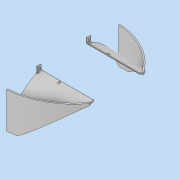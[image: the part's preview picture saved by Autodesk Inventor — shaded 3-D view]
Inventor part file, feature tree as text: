
AUTODESK INVENTOR PART (.ipt)
format: ipt  version: 2019 (Build 230136000, 136)  size: 896,000 bytes
history: native  units: mm
features: extrude x29, sketch x27, projected_geometry x12, fillet x5, other x4, mirror x3, loft x1, shell x1
ambient origin geometry x8: Origin, YZ Plane, XZ Plane, XY Plane, X Axis, Y Axis, Z Axis, Center Point
bodies: Body1 (feature_tree)
feature tree (82):
  sketch  "Эскиз4"
  other  "РабПлоскость1"
  sketch  "Эскиз5"
  loft  "Лофт1"
  extrude  "Выдавливание2"  Depth=100.0mm
  shell  "Оболочка1"  Thickness=17.0mm
  sketch  "Эскиз21"
  extrude  "Выдавливание15"  Depth=4.0mm
  extrude  "Выдавливание16"  Depth=35.0mm
  other  "РабПлоскость7"
  sketch  "Эскиз23"
  extrude  "Выдавливание17"  TaperAngle=0.0deg  [1 undecoded]
  extrude  "Выдавливание18"  TaperAngle=0.0deg  [1 undecoded]
  sketch  "Эскиз24"
  extrude  "Выдавливание19"  TaperAngle=0.0deg  [1 undecoded]
  extrude  "Выдавливание20"  Depth=130.0mm TaperAngle=0.0deg
  extrude  "Выдавливание21"  Depth=5.0mm
  mirror  "Зеркальное отражение2"
  other  "РабПлоскость12"
  extrude  "Выдавливание57"  Depth=2.0mm
  extrude  "Выдавливание62"  Depth=2.0mm
  mirror  "Зеркальное отражение5"
  extrude  "Выдавливание67"  Depth=2.0mm
  sketch  "Эскиз81"
  extrude  "Выдавливание68"  Depth=20.0mm
  extrude  "Выдавливание69"  Depth=10.0mm TaperAngle=0.0deg
  sketch  "Эскиз83"
  mirror  "Зеркальное отражение6"
  extrude  "Выдавливание70"  Depth=10.0mm TaperAngle=0.0deg
  sketch  "Эскиз84"
  extrude  "Выдавливание75"  Depth=143.802871mm
  extrude  "Выдавливание76"  TaperAngle=0.0deg  [1 undecoded]
  extrude  "Выдавливание77"  Depth=1.0mm TaperAngle=0.0deg
  extrude  "Выдавливание95"  Depth=5.0mm
  extrude  "Выдавливание96"  Depth=5.0mm
  extrude  "Выдавливание97"  Depth=2.0mm
  extrude  "Выдавливание98"  Depth=2.0mm
  extrude  "Выдавливание99"  Depth=5.0mm
  extrude  "Выдавливание100"  Depth=1.0mm TaperAngle=0.0deg
  extrude  "Выдавливание101"  Depth=3.0mm
  extrude  "Выдавливание102"  Depth=2.0mm
  extrude  "Выдавливание103"  Depth=6.0mm
  extrude  "Выдавливание104"  Depth=1.0mm TaperAngle=0.0deg
  fillet  "Сопряжение3"  Radius=2.0mm
  other  "РабПлоскость25"
  extrude  "Выдавливание105"  Depth=2.0mm
  extrude  "Выдавливание106"  Depth=2.0mm
  fillet  "Сопряжение4"  Radius=5.0mm
  fillet  "Сопряжение5"  Radius=1.0mm
  fillet  "Сопряжение6"  Radius=4.0mm
  fillet  "Сопряжение7"  Radius=2.0mm
  sketch  "Эскиз6"
  projected_geometry  "Спроецированная петля1"
  sketch  "Эскиз22"
  sketch  "Эскиз25"
  sketch  "Эскиз61"
  sketch  "Эскиз73"
  sketch  "Эскиз80"
  sketch  "Эскиз87"
  sketch  "Эскиз109"
  sketch  "Эскиз110"
  projected_geometry  "Спроецированная петля42"
  sketch  "Эскиз111"
  projected_geometry  "Спроецированная петля43"
  sketch  "Эскиз113"
  projected_geometry  "Спроецированная петля44"
  sketch  "Эскиз114"
  sketch  "Эскиз115"
  projected_geometry  "Спроецированная петля45"
  projected_geometry  "Спроецированная петля46"
  sketch  "Эскиз116"
  projected_geometry  "Спроецированная петля47"
  projected_geometry  "Спроецированная петля48"
  sketch  "Эскиз117"
  projected_geometry  "Спроецированная петля49"
  projected_geometry  "Спроецированная петля50"
  sketch  "Эскиз119"
  sketch  "Эскиз120"
  projected_geometry  "Спроецированная петля51"
  projected_geometry  "Спроецированная петля52"
  sketch  "Эскиз122"
  sketch  "Эскиз123"
note: 4 required parameter values undecoded (feature->parameter linkage not recoverable at this tier; creation-order binding heuristic only, values carry confidence <= 0.55)
